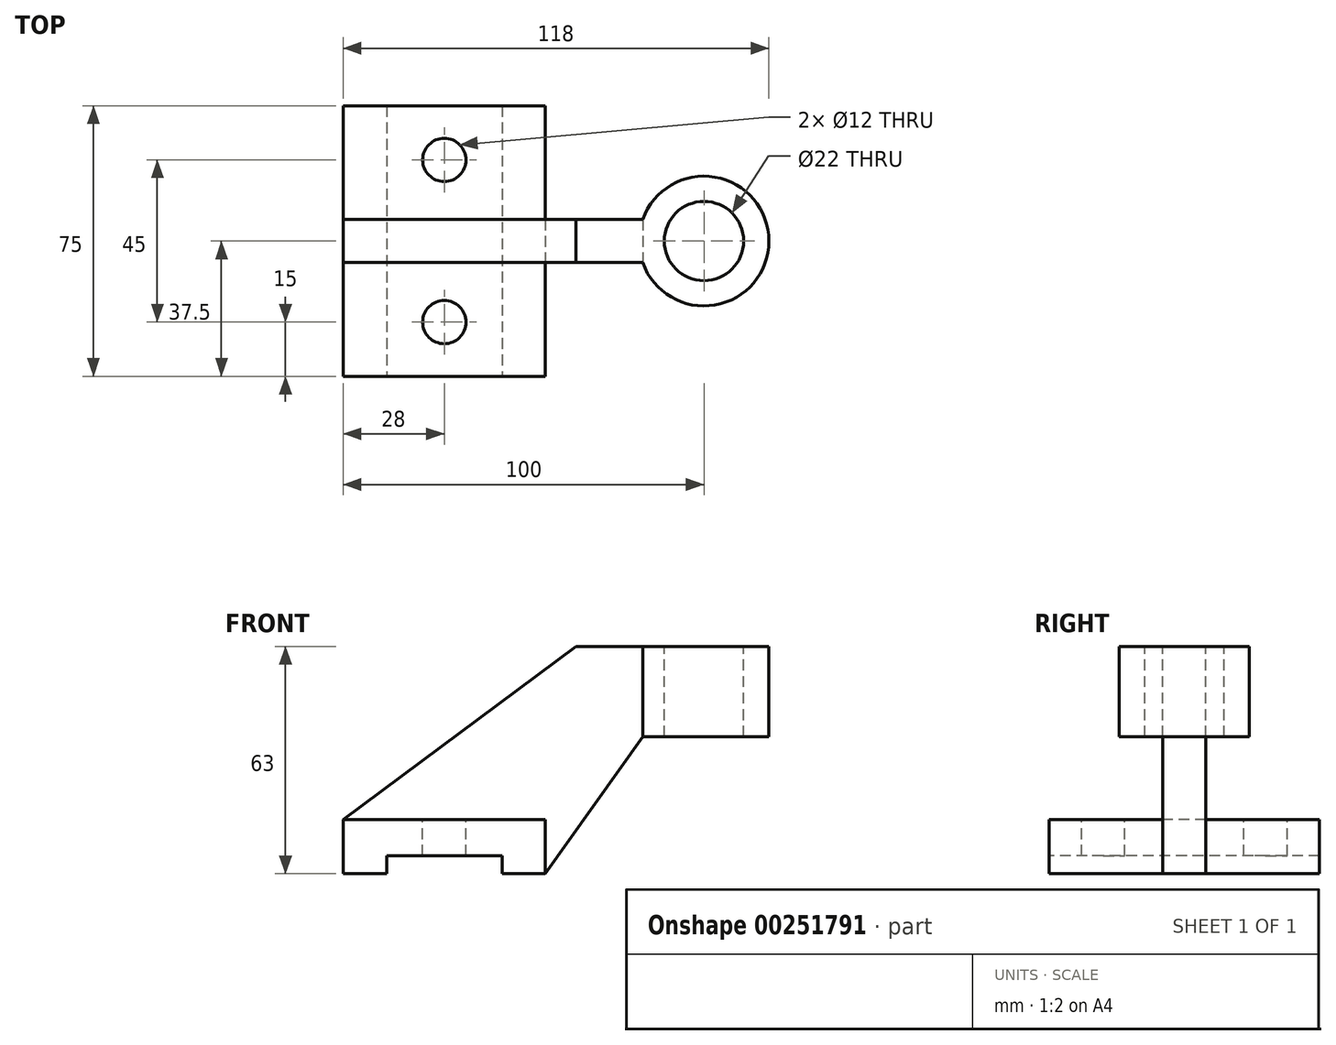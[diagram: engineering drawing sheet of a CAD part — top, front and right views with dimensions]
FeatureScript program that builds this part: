
annotation { "Feature Type Name" : "Feature", "Feature Type Description" : "" }
export const myFeature = defineFeature(function(context is Context, id is Id, definition is map)
    precondition{}
    {
        {
            var Q0;
            Q0=qCreatedBy(makeId("Front.planeOp"),FACE);
            var sketch = newSketch(context, id + "F0", { "sketchPlane" : qUnion([Q0])});
            skLineSegment(sketch, "E0.bottom", {"start": v(-28, -7.5) * mm, "end": v(28, -7.5) * mm});
            skLineSegment(sketch, "E0.top", {"start": v(-28, 7.5) * mm, "end": v(28, 7.5) * mm});
            skLineSegment(sketch, "E0.left", {"start": v(-28, -7.5) * mm, "end": v(-28, 7.5) * mm});
            skLineSegment(sketch, "E0.right", {"start": v(28, -7.5) * mm, "end": v(28, 7.5) * mm});
            skPoint(sketch, "E0.middle", {"position": v(0, 0) * mm});
            skSolve(sketch);
        }
        {
            var Q0;
            Q0 = qSketchRegion(id + "F0", true);
            extrude(context, id + "F1", {"entities" : qUnion([Q0]), "endBound" : BoundingType.SYMMETRIC, "depth" : 75 * mm});
        }
        {
            var Q0;
            Q0=makeQuery(id+"F1.opExtrude","CAP_FACE",FACE,{"disambiguationData":[OSD([sQuery(id+"F0.wireOp",EDGE,"E0.bottom"),sQuery(id+"F0.wireOp",EDGE,"E0.top"),sQuery(id+"F0.wireOp",EDGE,"E0.left"),sQuery(id+"F0.wireOp",EDGE,"E0.right")])],"isStart":false});
            var sketch = newSketch(context, id + "F2", { "sketchPlane" : qUnion([Q0])});
            skLineSegment(sketch, "E1.bottom", {"start": v(-16, -7.5) * mm, "end": v(16, -7.5) * mm});
            skLineSegment(sketch, "E1.top", {"start": v(-16, -2.5) * mm, "end": v(16, -2.5) * mm});
            skLineSegment(sketch, "E1.left", {"start": v(-16, -7.5) * mm, "end": v(-16, -2.5) * mm});
            skLineSegment(sketch, "E1.right", {"start": v(16, -7.5) * mm, "end": v(16, -2.5) * mm});
            skSolve(sketch);
        }
        {
            var Q0;
            Q0=makeQuery(id+"F1.opExtrude","SWEPT_FACE",FACE,{"disambiguationData":[OSD([sQuery(id+"F0.wireOp",EDGE,"E0.left")])]});
            var sketch = newSketch(context, id + "F3", { "sketchPlane" : qUnion([Q0])});
            skLineSegment(sketch, "E2.bottom", {"start": v(-6, -7.5) * mm, "end": v(6, -7.5) * mm});
            skLineSegment(sketch, "E2.top", {"start": v(-6, 55.5) * mm, "end": v(6, 55.5) * mm});
            skLineSegment(sketch, "E2.left", {"start": v(-6, -7.5) * mm, "end": v(-6, 55.5) * mm});
            skLineSegment(sketch, "E2.right", {"start": v(6, -7.5) * mm, "end": v(6, 55.5) * mm});
            skSolve(sketch);
        }
        {
            var Q0;
            Q0 = qSketchRegion(id + "F3", true);
            extrude(context, id + "F4", {"entities" : qUnion([Q0]), "operationType" : NewBodyOperationType.ADD, "oppositeDirection" : true, "depth" : 100 * mm});
        }
        {
            var Q0;
            {var subQ0=sQuery(id+"F3.wireOp",EDGE,"E2.right");Q0=makeQuery(id+"F4.boolean.opBoolean","SPLIT",FACE,{"disambiguationData":[TD([makeQuery(id+"F1.opExtrude","SWEPT_FACE",FACE,{"disambiguationData":[OSD([sQuery(id+"F0.wireOp",EDGE,"E0.top")])]})])],"derivedFrom":makeQuery(id+"F4.opExtrude","SWEPT_FACE",FACE,{"disambiguationData":[OSD([subQ0])]})});}
            var sketch = newSketch(context, id + "F5", { "sketchPlane" : qUnion([Q0])});
            skLineSegment(sketch, "E3", {"start": v(-28, 7.5) * mm, "end": v(36.45, 55.5) * mm});
            skLineSegment(sketch, "E4.0", {"start": v(36.45, 55.5) * mm, "end": v(-28, 55.5) * mm});
            skLineSegment(sketch, "E5.0", {"start": v(-28, 7.5) * mm, "end": v(-28, 55.5) * mm});
            skPoint(sketch, "E6.orphan", {"position": v(72, 55.5) * mm});
            skSolve(sketch);
        }
        {
            var Q0;
            Q0 = qSketchRegion(id + "F5", true);
            extrude(context, id + "F6", {"entities" : qUnion([Q0]), "operationType" : NewBodyOperationType.REMOVE, "endBound" : BoundingType.THROUGH_ALL, "oppositeDirection" : true, "depth" : 25 * mm});
        }
        {
            var Q0;
            Q0=makeQuery(id+"F4.opExtrude","SWEPT_FACE",FACE,{"disambiguationData":[OSD([sQuery(id+"F3.wireOp",EDGE,"E2.top")])]});
            var sketch = newSketch(context, id + "F7", { "sketchPlane" : qUnion([Q0])});
            skCircle(sketch, "E7", {"center": v(72, 0) * mm, "radius": 18 * mm});
            skSolve(sketch);
        }
        {
            var Q0;
            Q0 = qSketchRegion(id + "F7", true);
            extrude(context, id + "F8", {"entities" : qUnion([Q0]), "operationType" : NewBodyOperationType.ADD, "oppositeDirection" : true, "depth" : 25 * mm});
        }
        {
            var Q0;
            {var subQ0=sQuery(id+"F3.wireOp",EDGE,"E2.right");Q0=makeQuery(id+"F4.boolean.opBoolean","SPLIT",FACE,{"disambiguationData":[TD([makeQuery(id+"F1.opExtrude","SWEPT_FACE",FACE,{"disambiguationData":[OSD([sQuery(id+"F0.wireOp",EDGE,"E0.top")])]})])],"derivedFrom":makeQuery(id+"F4.opExtrude","SWEPT_FACE",FACE,{"disambiguationData":[OSD([subQ0])]})});}
            var sketch = newSketch(context, id + "F9", { "sketchPlane" : qUnion([Q0])});
            skLineSegment(sketch, "E8", {"start": v(28, -7.5) * mm, "end": v(55.03, 30.5) * mm});
            skLineSegment(sketch, "E9.0", {"start": v(72, -7.5) * mm, "end": v(72, 30.5) * mm});
            skLineSegment(sketch, "E10.0", {"start": v(72, -7.5) * mm, "end": v(28, -7.5) * mm});
            skLineSegment(sketch, "E11.0", {"start": v(55.03, 30.5) * mm, "end": v(72, 30.5) * mm});
            skPoint(sketch, "E12.orphan", {"position": v(90, 30.5) * mm});
            skSolve(sketch);
        }
        {
            var Q0;
            Q0 = qSketchRegion(id + "F9", true);
            extrude(context, id + "F10", {"entities" : qUnion([Q0]), "operationType" : NewBodyOperationType.REMOVE, "endBound" : BoundingType.THROUGH_ALL, "oppositeDirection" : true, "depth" : 25 * mm});
        }
        {
            var Q0;
            Q0=makeQuery(id+"F8.boolean.opBoolean","MERGE",FACE,{"derivedFrom":[makeQuery(id+"F4.opExtrude","SWEPT_FACE",FACE,{"disambiguationData":[OSD([sQuery(id+"F3.wireOp",EDGE,"E2.top")])]}),makeQuery(id+"F8.opExtrude","CAP_FACE",FACE,{"disambiguationData":[OSD([sQuery(id+"F7.wireOp",EDGE,"E7")])],"isStart":true})]});
            var sketch = newSketch(context, id + "F11", { "sketchPlane" : qUnion([Q0])});
            skCircle(sketch, "E13", {"center": v(72, 0) * mm, "radius": 11 * mm});
            skSolve(sketch);
        }
        {
            var Q0;
            Q0 = qSketchRegion(id + "F11", true);
            extrude(context, id + "F12", {"entities" : qUnion([Q0]), "operationType" : NewBodyOperationType.REMOVE, "endBound" : BoundingType.THROUGH_ALL, "oppositeDirection" : true, "depth" : 25 * mm});
        }
        {
            var Q0;
            Q0 = qSketchRegion(id + "F2", true);
            extrude(context, id + "F13", {"entities" : qUnion([Q0]), "operationType" : NewBodyOperationType.REMOVE, "endBound" : BoundingType.THROUGH_ALL, "oppositeDirection" : true, "depth" : 25 * mm});
        }
        {
            var Q0;
            {var subQ0=sQuery(id+"F3.wireOp",EDGE,"E2.left");var subQ3=sQuery(id+"F0.wireOp",EDGE,"E0.top");Q0=makeQuery(id+"F4.boolean.opBoolean","SPLIT",FACE,{"disambiguationData":[TD([makeQuery(id+"F4.opExtrude","SWEPT_FACE",FACE,{"disambiguationData":[OSD([subQ0])]})])],"derivedFrom":makeQuery(id+"F1.opExtrude","SWEPT_FACE",FACE,{"disambiguationData":[OSD([subQ3])]})});}
            var sketch = newSketch(context, id + "F14", { "sketchPlane" : qUnion([Q0])});
            skCircle(sketch, "E14", {"center": v(0, 22.5) * mm, "radius": 6 * mm});
            skCircle(sketch, "E15", {"center": v(0, -22.5) * mm, "radius": 6 * mm});
            skSolve(sketch);
        }
        {
            var Q0;
            Q0 = qSketchRegion(id + "F14", true);
            extrude(context, id + "F15", {"entities" : qUnion([Q0]), "operationType" : NewBodyOperationType.REMOVE, "endBound" : BoundingType.THROUGH_ALL, "oppositeDirection" : true, "depth" : 25 * mm});
        }
    });
